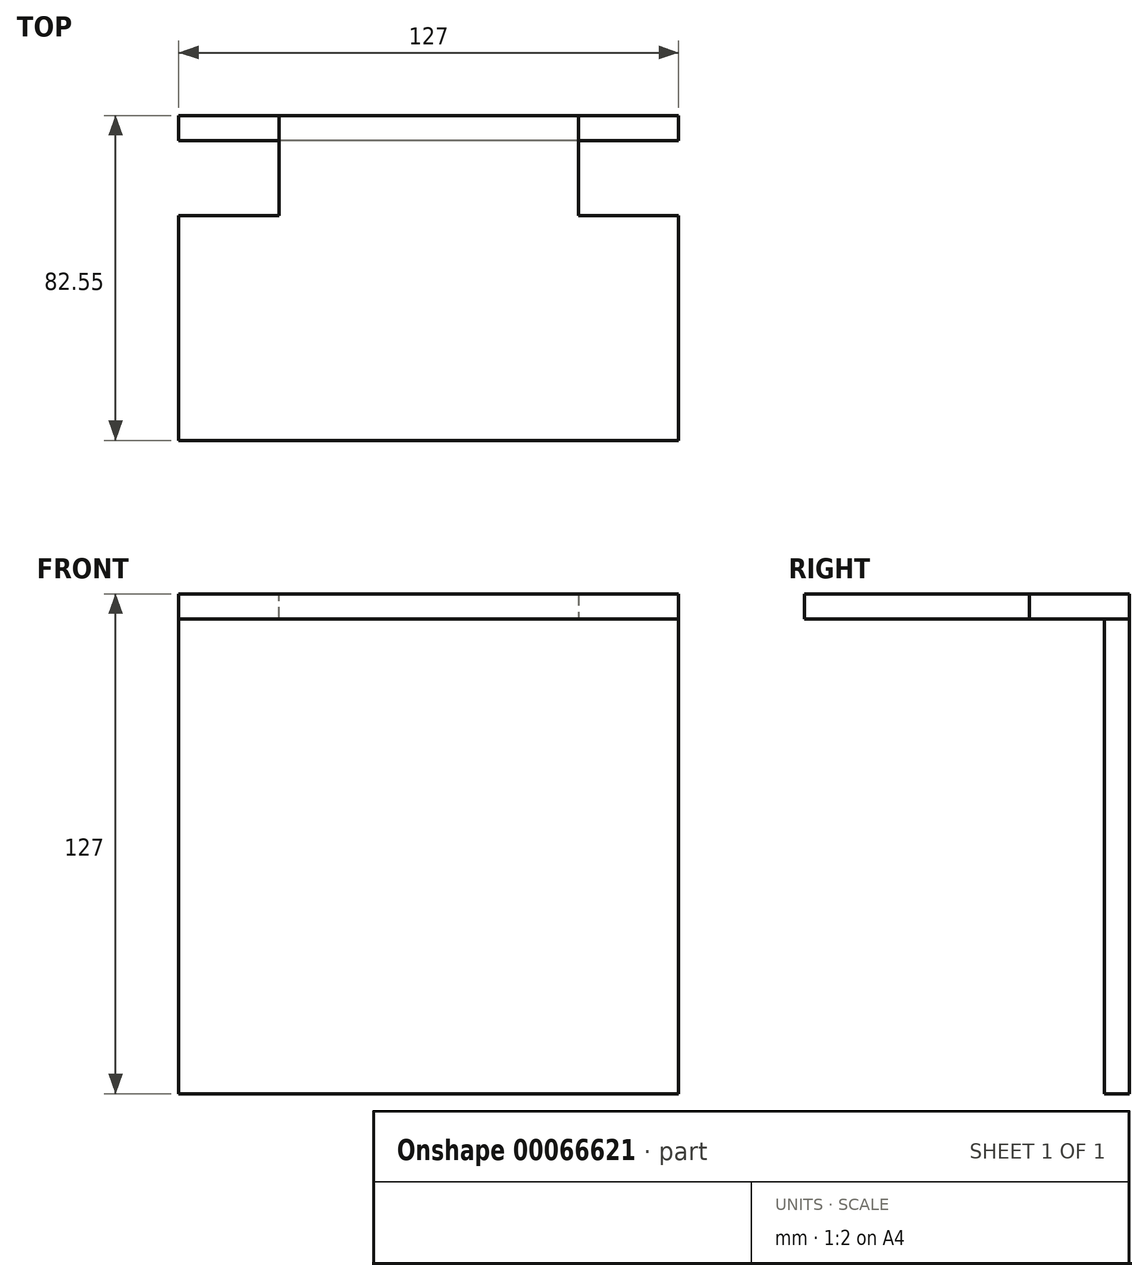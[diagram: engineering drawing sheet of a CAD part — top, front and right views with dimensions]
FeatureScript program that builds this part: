
annotation { "Feature Type Name" : "Feature", "Feature Type Description" : "" }
export const myFeature = defineFeature(function(context is Context, id is Id, definition is map)
    precondition{}
    {
        {
            var Q0;
            Q0=qCreatedBy(makeId("Front.planeOp"),FACE);
            var sketch = newSketch(context, id + "F0", { "sketchPlane" : qUnion([Q0])});
            skLineSegment(sketch, "E0.rect.bottom", {"start": v(63.5, 63.5) * mm, "end": v(-63.5, 63.5) * mm});
            skLineSegment(sketch, "E0.rect.top", {"start": v(63.5, -63.5) * mm, "end": v(-63.5, -63.5) * mm});
            skLineSegment(sketch, "E0.rect.left", {"start": v(63.5, 63.5) * mm, "end": v(63.5, -63.5) * mm});
            skLineSegment(sketch, "E0.rect.right", {"start": v(-63.5, 63.5) * mm, "end": v(-63.5, -63.5) * mm});
            skPoint(sketch, "E0.rect.middle", {"position": v(0, 0) * mm});
            skSolve(sketch);
        }
        {
            var Q0;
            Q0=makeQuery(id+"F0.imprint","IMPRINT",FACE,{"disambiguationData":[TD([[makeQuery(id+"F0.imprint","IMPRINT",EDGE,{"derivedFrom":sQuery(id+"F0.wireOp",EDGE,"E0.rect.bottom")}),1.0]])]});
            extrude(context, id + "F1", {"entities" : qUnion([Q0]), "depth" : 6.35 * mm});
        }
        {
            var Q0;
            Q0=makeQuery(id+"F1.opExtrude","SWEPT_FACE",FACE,{"disambiguationData":[OSD([sQuery(id+"F0.wireOp",EDGE,"E0.rect.bottom")])]});
            var sketch = newSketch(context, id + "F2", { "sketchPlane" : qUnion([Q0])});
            skLineSegment(sketch, "E1.bottom", {"start": v(-63.5, -6.35) * mm, "end": v(63.5, -6.35) * mm});
            skLineSegment(sketch, "E1.top", {"start": v(-63.5, -82.55) * mm, "end": v(63.5, -82.55) * mm});
            skLineSegment(sketch, "E1.left", {"start": v(-63.5, -6.35) * mm, "end": v(-63.5, -82.55) * mm});
            skLineSegment(sketch, "E1.right", {"start": v(63.5, -6.35) * mm, "end": v(63.5, -82.55) * mm});
            skSolve(sketch);
        }
        {
            var Q0;
            Q0=makeQuery(id+"F2.imprint","IMPRINT",FACE,{"disambiguationData":[TD([[makeQuery(id+"F2.imprint","IMPRINT",EDGE,{"derivedFrom":sQuery(id+"F2.wireOp",EDGE,"E1.bottom")}),1.0]])]});
            extrude(context, id + "F3", {"entities" : qUnion([Q0]), "oppositeDirection" : true, "depth" : 6.35 * mm});
        }
        {
            var Q0;
            Q0=makeQuery(id+"F3.opExtrude","CAP_FACE",FACE,{"disambiguationData":[OSD([sQuery(id+"F2.wireOp",EDGE,"E1.bottom"),sQuery(id+"F2.wireOp",EDGE,"E1.top"),sQuery(id+"F2.wireOp",EDGE,"E1.left"),sQuery(id+"F2.wireOp",EDGE,"E1.right")])],"isStart":true});
            var sketch = newSketch(context, id + "F4", { "sketchPlane" : qUnion([Q0])});
            skLineSegment(sketch, "E2.bottom", {"start": v(63.5, -6.35) * mm, "end": v(38.1, -6.35) * mm});
            skLineSegment(sketch, "E2.top", {"start": v(63.5, 0) * mm, "end": v(38.1, 0) * mm});
            skLineSegment(sketch, "E2.left", {"start": v(63.5, -6.35) * mm, "end": v(63.5, 0) * mm});
            skLineSegment(sketch, "E2.right", {"start": v(38.1, -6.35) * mm, "end": v(38.1, 0) * mm});
            skLineSegment(sketch, "E3.bottom", {"start": v(-63.5, -6.35) * mm, "end": v(-38.1, -6.35) * mm});
            skLineSegment(sketch, "E3.top", {"start": v(-63.5, 0) * mm, "end": v(-38.1, 0) * mm});
            skLineSegment(sketch, "E3.left", {"start": v(-63.5, -6.35) * mm, "end": v(-63.5, 0) * mm});
            skLineSegment(sketch, "E3.right", {"start": v(-38.1, -6.35) * mm, "end": v(-38.1, 0) * mm});
            skSolve(sketch);
        }
        {
            var Q0;
            Q0=makeQuery(id+"F4.imprint","IMPRINT",FACE,{"disambiguationData":[TD([[makeQuery(id+"F4.imprint","IMPRINT",EDGE,{"derivedFrom":sQuery(id+"F4.wireOp",EDGE,"E3.bottom")}),-1.0]])]});
            var Q1;
            Q1=makeQuery(id+"F4.imprint","IMPRINT",FACE,{"disambiguationData":[TD([[makeQuery(id+"F4.imprint","IMPRINT",EDGE,{"derivedFrom":sQuery(id+"F4.wireOp",EDGE,"E2.bottom")}),-1.0]])]});
            var Q2;
            Q2=makeQuery(id+"F3.opExtrude","CAP_FACE",FACE,{"disambiguationData":[OSD([sQuery(id+"F2.wireOp",EDGE,"E1.bottom"),sQuery(id+"F2.wireOp",EDGE,"E1.top"),sQuery(id+"F2.wireOp",EDGE,"E1.left"),sQuery(id+"F2.wireOp",EDGE,"E1.right")])],"isStart":false});
            extrude(context, id + "F5", {"entities" : qUnion([Q0, Q1]), "operationType" : NewBodyOperationType.ADD, "endBound" : BoundingType.UP_TO_SURFACE, "oppositeDirection" : true, "endBoundEntityFace" : qUnion([Q2]), "depth" : 25.4 * mm});
        }
        {
            var Q0;
            Q0=makeQuery(id+"F1.opExtrude","CAP_FACE",FACE,{"disambiguationData":[OSD([sQuery(id+"F0.wireOp",EDGE,"E0.rect.bottom"),sQuery(id+"F0.wireOp",EDGE,"E0.rect.top"),sQuery(id+"F0.wireOp",EDGE,"E0.rect.left"),sQuery(id+"F0.wireOp",EDGE,"E0.rect.right")])],"isStart":true});
            var sketch = newSketch(context, id + "F6", { "sketchPlane" : qUnion([Q0])});
            skLineSegment(sketch, "E4.bottom", {"start": v(-63.5, 63.5) * mm, "end": v(-38.1, 63.5) * mm, "construction": true});
            skLineSegment(sketch, "E4.top", {"start": v(-63.5, 57.15) * mm, "end": v(-38.1, 57.15) * mm, "construction": true});
            skLineSegment(sketch, "E4.left", {"start": v(-63.5, 63.5) * mm, "end": v(-63.5, 57.15) * mm, "construction": true});
            skLineSegment(sketch, "E4.right", {"start": v(-38.1, 63.5) * mm, "end": v(-38.1, 57.15) * mm, "construction": true});
            skLineSegment(sketch, "E5.bottom", {"start": v(38.1, 57.15) * mm, "end": v(63.5, 57.15) * mm, "construction": true});
            skLineSegment(sketch, "E5.top", {"start": v(38.1, 63.5) * mm, "end": v(63.5, 63.5) * mm, "construction": true});
            skLineSegment(sketch, "E5.left", {"start": v(38.1, 57.15) * mm, "end": v(38.1, 63.5) * mm, "construction": true});
            skLineSegment(sketch, "E5.right", {"start": v(63.5, 57.15) * mm, "end": v(63.5, 63.5) * mm, "construction": true});
            skLineSegment(sketch, "E6.0", {"start": v(-63.55, 57.1) * mm, "end": v(-38.05, 57.1) * mm});
            skLineSegment(sketch, "E6.1", {"start": v(-63.55, 63.55) * mm, "end": v(-63.55, 57.1) * mm});
            skLineSegment(sketch, "E6.2", {"start": v(-63.55, 63.55) * mm, "end": v(-38.05, 63.55) * mm});
            skLineSegment(sketch, "E6.3", {"start": v(-38.05, 63.55) * mm, "end": v(-38.05, 57.1) * mm});
            skLineSegment(sketch, "E7.0", {"start": v(38.05, 57.1) * mm, "end": v(63.55, 57.1) * mm});
            skLineSegment(sketch, "E7.1", {"start": v(38.05, 57.1) * mm, "end": v(38.05, 63.55) * mm});
            skLineSegment(sketch, "E7.2", {"start": v(38.05, 63.55) * mm, "end": v(63.55, 63.55) * mm});
            skLineSegment(sketch, "E7.3", {"start": v(63.55, 57.1) * mm, "end": v(63.55, 63.55) * mm});
            skSolve(sketch);
        }
        {
            var Q0;
            Q0 = qSketchRegion(id + "F6", true);
            extrude(context, id + "F7", {"entities" : qUnion([Q0]), "operationType" : NewBodyOperationType.REMOVE, "oppositeDirection" : true, "depth" : 25.4 * mm});
        }
    });
